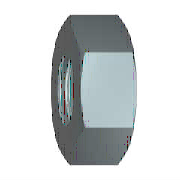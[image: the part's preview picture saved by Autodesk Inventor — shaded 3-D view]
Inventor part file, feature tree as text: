
AUTODESK INVENTOR PART (.ipt)
format: ipt  version: 2015 (Build 190159000, 159)  size: 162,304 bytes
history: native  units: mm (DEFAULTED — no unit token found)
features: sketch x3, chamfer x1, hole x1, other x1, plane x1
ambient origin geometry x7: Origin, YZ Plane, XZ Plane, X Axis, Y Axis, Z Axis, Center Point
bodies: Solid1 (feature_tree), Body (feature_tree)
feature tree (7):
  chamfer  "Chamfer1"  Angle=30.0deg  [1 undecoded]
  hole  "Thread"  [1 undecoded]
  other  "Work Axis1"
  plane  "Work Plane1"
  sketch  "Sketch1"  dims[d0=6.928203mm]
  sketch  "Sketch2"  dims[d1=2.8mm]
  sketch  "Sketch3"  dims[d2=0.0mm d3=30.0deg d4=30.0deg d5=5.0mm d6=5.0mm d7=90.0deg d25=2.85mm d26=6.0mm d27=4.0mm d28=2.0mm d29=14.3117mm d30=8.0mm d31=20.594885mm d8=0.32476mm d9=30.0deg d10=0.32476mm d11=30.0deg d13=0.0mm d14=0.0mm d39=0.0mm d40=0.32476mm d41=0.32476mm d42=0.0mm]
note: 2 required parameter values undecoded (feature->parameter linkage not recoverable at this tier; creation-order binding heuristic only, values carry confidence <= 0.55)
